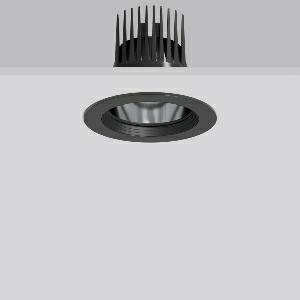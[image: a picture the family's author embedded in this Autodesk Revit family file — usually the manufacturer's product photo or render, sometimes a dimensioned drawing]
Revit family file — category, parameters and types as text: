
# Revit family: heledon_maxi_e_901758_003_3_76_54b1
name_source: partatom
category: Lighting Fixtures
units: mm (PartAtom-declared; Revit-internal decimal feet)

## family parameters
Cut with Voids When Loaded = No
Host = Face
Light Source = No
Part Type = Normal
Room Calculation Point = No
Round Connector Dimension = Use Diameter
Shared = No

## types (1)
- HELEDON maxi E (1 x LED Modul 935, 3400 lm, 3500)
    Apparent Load = 25 VA
    Approval mark = CE
    CIE Flux Codes = 100 100 100 100 100
    Color Rendering = 92
    Color Temperature = 3500
    Default Elevation = 1800 mm
    Description = Series: HELEDON maxi
Round recessed downlight. Housing: die-cast aluminium, powder-coated. Black plastic ring and recessed LED to prevent glare from the side. Optical assembly with reflector made of MIRO-Silver with 98% total light reflection for outstanding efficiency - can be changed without tools. Best colour rendering index Ra>90. Suitable for Recessed ceiling mounting. Installation without tools thanks to spring fastening system. Including separate LED converter with connecting cable 600 mm.High quality converter without flickering and stroboscopic effect. Through-wiring box (5 pole) available as accessory. The following accessories can be mounted without use of tools: interchangeable lenses, decorative glasses, honeycomb louvre, clear and frosted diffusers, white interchangeable plastic ring. 
Colour: deep black, matt (RAL 9005)
Diameter: 162 mm
Height: 3 mm
Cut-out diameter: 152 mm
Recess height: 200 mm
Luminaire: recess height: 135 mm
Lamp: LED
Socket: without socket
Colour temperature: 3500K
Colour rendering index (CRI): 92
System power: 25 W
Rated luminous flux: 3400 lm
Luminous efficiency: 136 lm/W
Control gear: Converter, dimmable, DALI
Protection class: II
Type of protection: IP 20
    Height = 0 mm  [stored 0 ft]
    Lamp = 1 x LED Modul 935
    Lamp Light Flux = 3400 lm
    Lamp count = 1
    Length = 162 mm
    Lifetime = 50000 h
    Luminous efficacy = 136 lm/W
    Manufacturer = RZB
    ModVariant = No
    Model = 901758.003.3.76
    Mounting Place = Ceiling
    Mounting Type = Recessed
    Number of Poles = 1
    OnlyDefault = Yes
    Power Factor = 1
    Product Name = HELEDON maxi E
    Product group = Recessed downlights
    ProductGroupID = 402
    Protection Class = Protection class II
    Protection Degree = IP 20
    RLX_Detail_Level = 1
    RLX_Emergency_Light_Flux = 0 lm
    RLX_Emergency_Type = 0
    RLX_Emergency_Type_DB = No
    RlxData = <blob elided: 121701 chars, md5=7a0b8ac6>
    Socket = socket
    Standby Power = 0 W
    System Light Flux = 3400 lm
    System Power = 25 W
    Type Comments = Product without accessories
    Type Image = 901662.003.jpg
    URL = http://relux.com
    VarID = ---
    Voltage = 230 V
    Voltage Range = 220-240 V
    Weight = 0.00 kg
    Width = 0 mm  [stored 0 ft]

note: [stored X ft] marks values corroborated as IEEE doubles in the binary element streams (Revit-internal decimal feet)

## geometry (parser evidence)
native form markers: Blend x4, Sweep x12
no freeform markers — native parametric forms only
